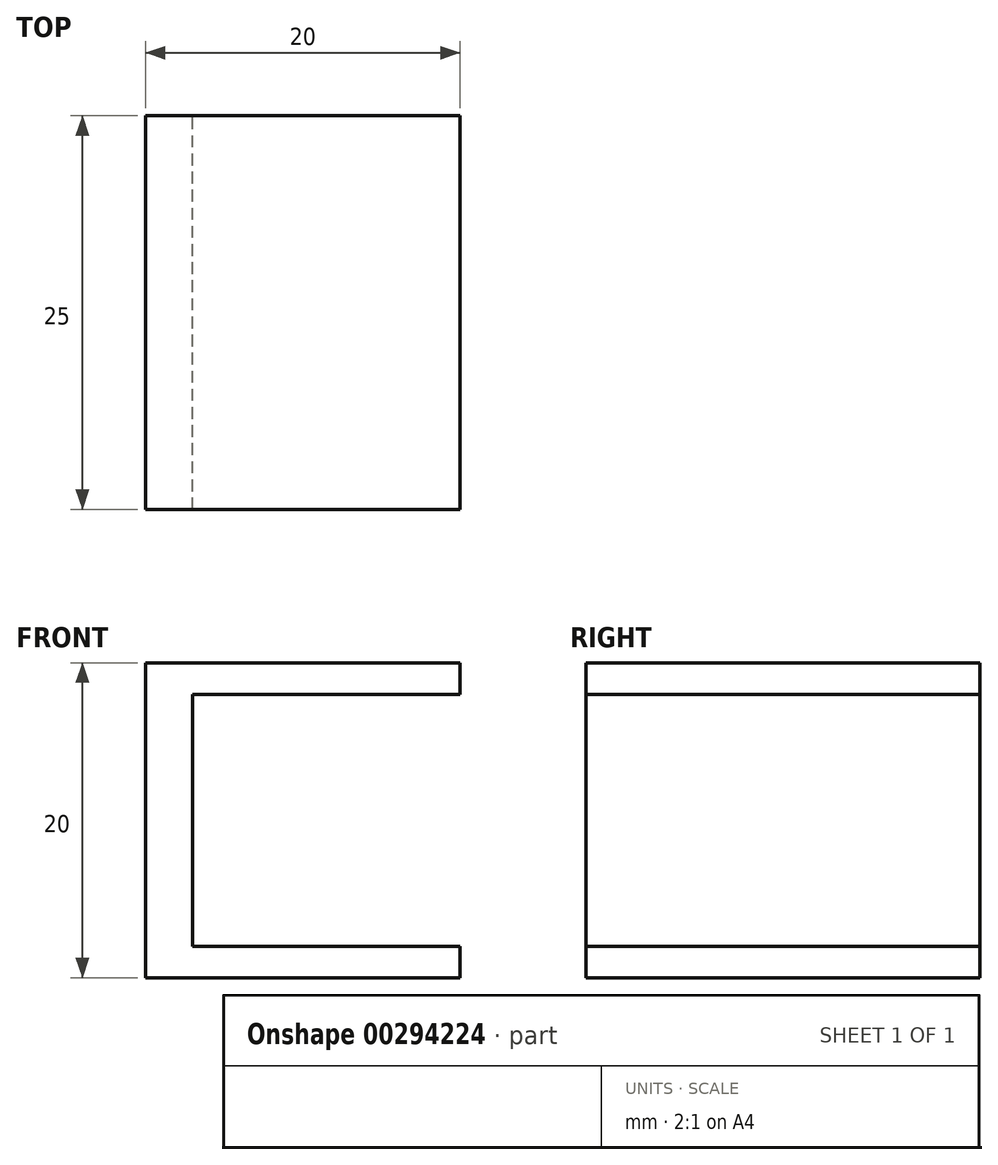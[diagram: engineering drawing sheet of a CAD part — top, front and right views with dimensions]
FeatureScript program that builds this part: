
annotation { "Feature Type Name" : "Feature", "Feature Type Description" : "" }
export const myFeature = defineFeature(function(context is Context, id is Id, definition is map)
    precondition{}
    {
        {
            var Q0;
            Q0=qCreatedBy(makeId("Front.planeOp"),FACE);
            var sketch = newSketch(context, id + "F0", { "sketchPlane" : qUnion([Q0])});
            skLineSegment(sketch, "E0.bottom", {"start": v(10, 10) * mm, "end": v(-10, 10) * mm});
            skLineSegment(sketch, "E0.top", {"start": v(10, -10) * mm, "end": v(-10, -10) * mm});
            skLineSegment(sketch, "E0.left", {"start": v(10, 10) * mm, "end": v(10, 8) * mm});
            skLineSegment(sketch, "E0.right", {"start": v(-10, 10) * mm, "end": v(-10, -10) * mm});
            skPoint(sketch, "E0.middle", {"position": v(0, 0) * mm});
            skLineSegment(sketch, "E1", {"start": v(10, 8) * mm, "end": v(-7, 8) * mm});
            skLineSegment(sketch, "E2", {"start": v(-7, 8) * mm, "end": v(-7, -8) * mm});
            skLineSegment(sketch, "E3", {"start": v(-7, -8) * mm, "end": v(10, -8) * mm});
            skPoint(sketch, "E4.endSnap0", {"position": v(-10, 0) * mm});
            skLineSegment(sketch, "E5.trimOffspring", {"start": v(10, -8) * mm, "end": v(10, -10) * mm});
            skPoint(sketch, "E6.end.orphan", {"position": v(-10, 6) * mm});
            skPoint(sketch, "E4.end.orphan", {"position": v(-10, -6) * mm});
            skSolve(sketch);
        }
        {
            var Q0;
            Q0 = qSketchRegion(id + "F0", true);
            extrude(context, id + "F1", {"entities" : qUnion([Q0]), "depth" : 25 * mm});
        }
    });
